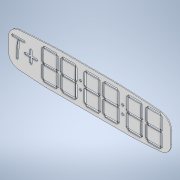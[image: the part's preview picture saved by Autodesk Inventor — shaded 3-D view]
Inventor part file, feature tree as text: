
AUTODESK INVENTOR PART (.ipt)
format: ipt  version: 2021 (Build 250183000, 183)  size: 840,192 bytes
history: native  units: in
note: dims shown in document units (in); Inventor stores cm internally (conversion verified against a paired STEP export)
features: other x30, extrude x2, sketch x1
ambient origin geometry x8: Origin, YZ Plane, XZ Plane, XY Plane, X Axis, Y Axis, Z Axis, Center Point
bodies: Solid1 (feature_tree)
feature tree (33):
  other  "Blocks"
  extrude  "Extrusion1"  TaperAngle=135.0deg  [1 undecoded]
  extrude  "Extrusion2"  Depth=1.9685in
  sketch  "Sketch4"  dims[d0=23.622in d2=11.811in d4=4.7244in d5=4.7244in d10=62.9921in d11=78.7402in d12=5.5118in d13=5.5118in d14=7.874in d15=7.874in d16=7.874in d17=12.5984in d18=5.6299in d19=0.3937in d20=0.3937in d21=0.5118in d22=0.5118in d23=2.9528in d24=1.6535in d25=1.5748in d26=1.5748in d27=1.6535in d28=0.7874in d29=0.1181in d30=0.0in d105=0.126in d108=0.126in d111=0.126in d112=0.126in d113=0.126in d114=0.126in d115=0.126in d116=0.0394in d117=0.315in d118=0.315in d121=0.126in d122=0.126in d123=1.9685in d126=135.0deg d127=1.9685in d128=135.0deg d129=0.1575in d130=0.1575in d131=0.0433in d132=0.0433in d137=0.0433in d138=0.0433in d139=0.0433in d140=0.0433in d141=0.0433in d142=0.0433in d143=0.0433in d144=0.0433in d145=0.0433in d146=0.0433in d150=0.0433in d151=0.0433in d152=0.0433in d153=0.0433in d244=0.0in d246=0.0in d247=0.0in d248=0.0in d249=0.3937in d250=0.2953in d251=0.9843in d252=0.2953in d253=0.9843in d259=0.126in d260=0.126in d261=0.126in d262=0.126in d263=0.126in d264=0.126in d265=0.126in d266=0.126in d267=0.126in d268=0.126in d269=0.126in d270=0.126in d271=0.126in d272=0.0in d273=0.0in d274=0.315in d275=0.315in d276=0.0in d277=0.0in d278=0.126in d279=0.126in d280=0.126in d281=90.0deg d284=0.6929in d285=0.6929in d286=0.6929in d287=0.6929in d288=0.6929in d289=0.0in d290=0.6929in d292=0.0394in d293=0.0394in d294=0.126in d295=0.126in d296=0.315in d297=0.126in d298=0.126in d299=2.2441in d304=0.126in d305=0.126in d306=0.126in d307=0.126in d308=0.0433in d309=0.8268in d310=0.8268in d311=0.126in d312=0.126in d314=0.126in d315=0.126in d316=0.126in d317=0.126in d318=0.126in d319=0.126in d320=0.0787in d321=0.0787in d322=0.0787in d323=0.0787in d324=0.8268in d325=0.0in d326=0.8268in d327=0.8268in d328=0.0in d329=0.8268in d330=1.5354in d334=0.0in d335=0.7087in d336=0.9055in d339=0.4528in d341=0.4528in d342=0.4528in d343=0.0in d344=0.4528in d346=0.1181in d347=0.0in]
  other  "Single Segment"
  other  "7 Segment Digit"
  other  "Slanted Segment Large"
  other  "+ sign"
  other  "Dot"
  other  "Clock Face with T +-"
  other  "Clock Front Face Outline"
  other  "Single Segment:9"
  other  "Single Segment:10"
  other  "Single Segment:11"
  other  "Single Segment:12"
  other  "Single Segment:13"
  other  "Single Segment:14"
  other  "Single Segment:15"
  other  "Clock Face with T +-:1"
  other  "7 Segment Digit:8"
  other  "7 Segment Digit:9"
  other  "7 Segment Digit:10"
  other  "7 Segment Digit:11"
  other  "7 Segment Digit:12"
  other  "Single Segment:21"
  other  "7 Segment Digit:13"
  other  "Slanted Segment Large:2"
  other  "+ sign:2"
  other  "Dot:7"
  other  "Dot:8"
  other  "Dot:9"
  other  "Dot:10"
  other  "Clock Front Face Outline:1"
note: 1 required parameter value undecoded (feature->parameter linkage not recoverable at this tier; creation-order binding heuristic only, values carry confidence <= 0.55)
